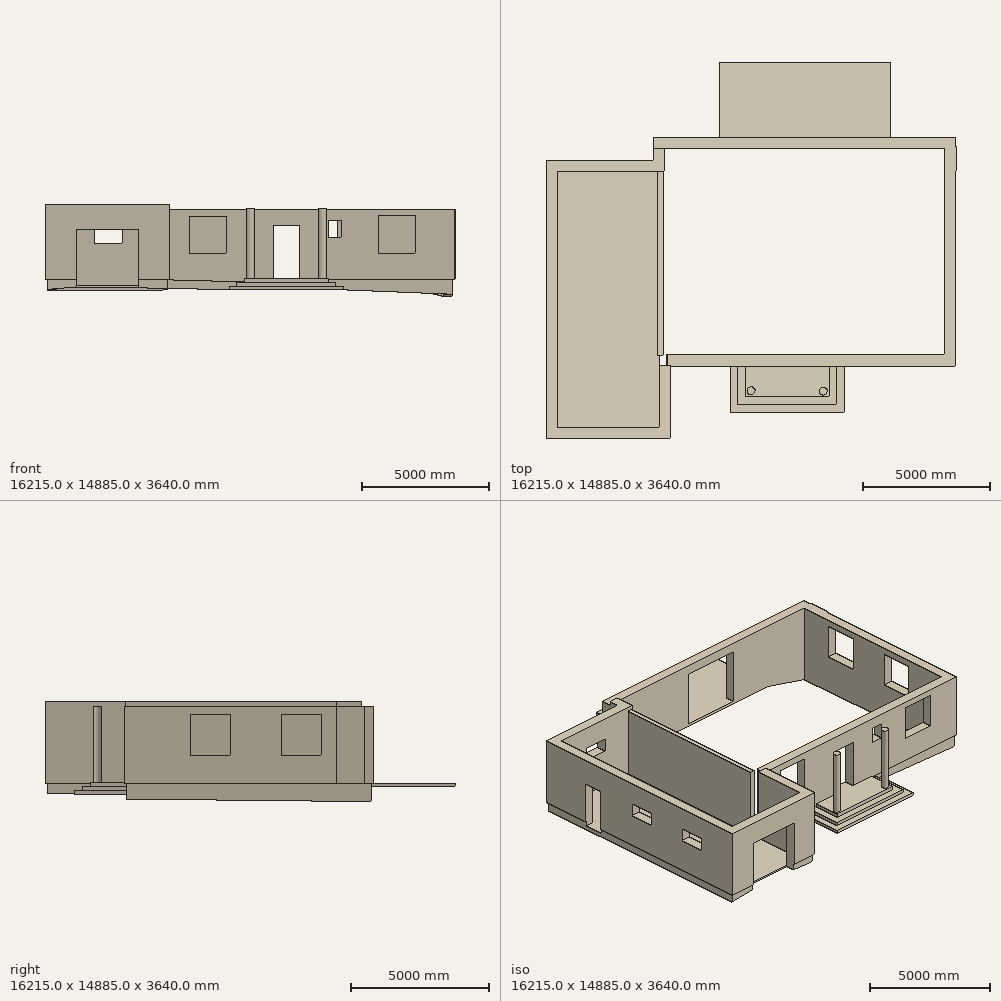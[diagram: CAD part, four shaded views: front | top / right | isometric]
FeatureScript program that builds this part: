
annotation { "Feature Type Name" : "Feature", "Feature Type Description" : "" }
export const myFeature = defineFeature(function(context is Context, id is Id, definition is map)
    precondition{}
    {
        {
            var Q0;
            Q0=qCreatedBy(makeId("Front.planeOp"),FACE);
            var sketch = newSketch(context, id + "F0", { "sketchPlane" : qUnion([Q0])});
            skLineSegment(sketch, "E0.bottom", {"start": v(0, 0) * mm, "end": v(70, 0) * mm});
            skLineSegment(sketch, "E0.top", {"start": v(0, 2980) * mm, "end": v(4455, 2980) * mm});
            skLineSegment(sketch, "E0.left", {"start": v(0, 0) * mm, "end": v(0, 2980) * mm});
            skLineSegment(sketch, "E0.right", {"start": v(4455, 0) * mm, "end": v(4455, 2980) * mm});
            skLineSegment(sketch, "E1.bottom", {"start": v(1245, 1990) * mm, "end": v(3685, 1990) * mm});
            skLineSegment(sketch, "E1.top", {"start": v(1245, -180) * mm, "end": v(3685, -180) * mm});
            skLineSegment(sketch, "E1.left", {"start": v(1245, 1990) * mm, "end": v(1245, 0) * mm});
            skLineSegment(sketch, "E1.right", {"start": v(3685, 1990) * mm, "end": v(3685, 0) * mm});
            skLineSegment(sketch, "E2", {"start": v(1245, 0) * mm, "end": v(1245, -180) * mm});
            skLineSegment(sketch, "E3", {"start": v(3685, 0) * mm, "end": v(4455, 0) * mm});
            skLineSegment(sketch, "E4", {"start": v(3685, 0) * mm, "end": v(3685, -180) * mm});
            skLineSegment(sketch, "E5", {"start": v(70, -380) * mm, "end": v(1245, -280) * mm});
            skLineSegment(sketch, "E6", {"start": v(1245, -280) * mm, "end": v(1245, -180) * mm});
            skLineSegment(sketch, "E7", {"start": v(3685, -180) * mm, "end": v(3685, -300) * mm});
            skLineSegment(sketch, "E8", {"start": v(3685, -300) * mm, "end": v(4455, -350) * mm});
            skLineSegment(sketch, "E9", {"start": v(70, 0) * mm, "end": v(1245, 0) * mm});
            skLineSegment(sketch, "E10", {"start": v(70, 0) * mm, "end": v(70, -380) * mm});
            skLineSegment(sketch, "E11", {"start": v(4455, 0) * mm, "end": v(4455, -350) * mm});
            skSolve(sketch);
        }
        {
            var Q0;
            Q0=makeQuery(id+"F0.imprint","IMPRINT",FACE,{"disambiguationData":[TD([[makeQuery(id+"F0.imprint","IMPRINT",EDGE,{"derivedFrom":sQuery(id+"F0.wireOp",EDGE,"E0.bottom")}),1.0]])]});
            extrude(context, id + "F1", {"entities" : qUnion([Q0]), "depth" : 440 * mm});
        }
        {
            var Q0;
            Q0=makeQuery(id+"F0.imprint","IMPRINT",FACE,{"disambiguationData":[TD([[makeQuery(id+"F0.imprint","IMPRINT",EDGE,{"derivedFrom":sQuery(id+"F0.wireOp",EDGE,"E2")}),-1.0]])]});
            var Q1;
            Q1=makeQuery(id+"F0.imprint","IMPRINT",FACE,{"disambiguationData":[TD([[makeQuery(id+"F0.imprint","IMPRINT",EDGE,{"derivedFrom":sQuery(id+"F0.wireOp",EDGE,"E3")}),-1.0]])]});
            extrude(context, id + "F2", {"entities" : qUnion([Q0, Q1]), "operationType" : NewBodyOperationType.ADD, "depth" : 370 * mm});
        }
        {
            var Q0;
            Q0=makeQuery(id+"F2.opExtrude","SWEPT_FACE",FACE,{"disambiguationData":[OSD([sQuery(id+"F0.wireOp",EDGE,"E10")])]});
            var sketch = newSketch(context, id + "F3", { "sketchPlane" : qUnion([Q0])});
            skLineSegment(sketch, "E12.bottom", {"start": v(440, 2980) * mm, "end": v(-10130, 2980) * mm});
            skLineSegment(sketch, "E12.top", {"start": v(440, 0) * mm, "end": v(-7385, 0) * mm});
            skLineSegment(sketch, "E12.left", {"start": v(440, 2980) * mm, "end": v(440, 0) * mm});
            skLineSegment(sketch, "E12.right", {"start": v(-10130, 2980) * mm, "end": v(-10130, 0) * mm});
            skLineSegment(sketch, "E13", {"start": v(-8275, 0) * mm, "end": v(-10130, 0) * mm});
            skLineSegment(sketch, "E14.bottom", {"start": v(-2510, 2005) * mm, "end": v(-1400, 2005) * mm});
            skLineSegment(sketch, "E14.top", {"start": v(-2510, 1445) * mm, "end": v(-1400, 1445) * mm});
            skLineSegment(sketch, "E14.left", {"start": v(-2510, 2005) * mm, "end": v(-2510, 1445) * mm});
            skLineSegment(sketch, "E14.right", {"start": v(-1400, 2005) * mm, "end": v(-1400, 1445) * mm});
            skLineSegment(sketch, "E15.bottom", {"start": v(-5475, 2005) * mm, "end": v(-4365, 2005) * mm});
            skLineSegment(sketch, "E15.top", {"start": v(-5475, 1445) * mm, "end": v(-4365, 1445) * mm});
            skLineSegment(sketch, "E15.left", {"start": v(-5475, 2005) * mm, "end": v(-5475, 1445) * mm});
            skLineSegment(sketch, "E15.right", {"start": v(-4365, 2005) * mm, "end": v(-4365, 1445) * mm});
            skLineSegment(sketch, "E16", {"start": v(-8275, 0) * mm, "end": v(-8275, 1850) * mm});
            skLineSegment(sketch, "E17", {"start": v(-8275, 1850) * mm, "end": v(-7385, 1850) * mm});
            skLineSegment(sketch, "E18", {"start": v(-7385, 1850) * mm, "end": v(-7385, 0) * mm});
            skLineSegment(sketch, "E19", {"start": v(-8275, 0) * mm, "end": v(-8275, -220) * mm});
            skLineSegment(sketch, "E20", {"start": v(-8275, -220) * mm, "end": v(-7385, -220) * mm});
            skLineSegment(sketch, "E21", {"start": v(-7385, -220) * mm, "end": v(-7385, 0) * mm});
            skLineSegment(sketch, "E22", {"start": v(0, -380) * mm, "end": v(-10130, -410) * mm});
            skLineSegment(sketch, "E23", {"start": v(-10130, -410) * mm, "end": v(-10130, 0) * mm});
            skSolve(sketch);
        }
        {
            var Q0;
            Q0=makeQuery(id+"F3.imprint","IMPRINT",FACE,{"disambiguationData":[TD([[makeQuery(id+"F3.imprint","IMPRINT",EDGE,{"derivedFrom":sQuery(id+"F3.wireOp",EDGE,"E12.bottom")}),1.0]])]});
            extrude(context, id + "F4", {"entities" : qUnion([Q0]), "operationType" : NewBodyOperationType.ADD, "oppositeDirection" : true, "depth" : 370 * mm, "hasSecondDirection" : true, "secondDirectionOppositeDirection" : false, "secondDirectionDepth" : 70 * mm});
        }
        {
            var Q0;
            Q0=makeQuery(id+"F3.imprint","IMPRINT",FACE,{"disambiguationData":[TD([[makeQuery(id+"F3.imprint","IMPRINT",EDGE,{"derivedFrom":sQuery(id+"F3.wireOp",EDGE,"E13")}),1.0]])]});
            extrude(context, id + "F5", {"entities" : qUnion([Q0]), "operationType" : NewBodyOperationType.ADD, "oppositeDirection" : true, "depth" : 370 * mm});
        }
        {
            var Q0;
            Q0=makeQuery(id+"F5.boolean.opBoolean","MERGE",FACE,{"derivedFrom":[makeQuery(id+"F4.opExtrude","SWEPT_FACE",FACE,{"disambiguationData":[OSD([sQuery(id+"F3.wireOp",EDGE,"E12.right")])]}),makeQuery(id+"F5.opExtrude","SWEPT_FACE",FACE,{"disambiguationData":[OSD([sQuery(id+"F3.wireOp",EDGE,"E23")])]})]});
            var sketch = newSketch(context, id + "F6", { "sketchPlane" : qUnion([Q0])});
            skLineSegment(sketch, "E24.bottom", {"start": v(0, 2980) * mm, "end": v(-4225, 2980) * mm});
            skLineSegment(sketch, "E24.top", {"start": v(0, 0) * mm, "end": v(-70, 0) * mm});
            skLineSegment(sketch, "E24.left", {"start": v(0, 2980) * mm, "end": v(0, 0) * mm});
            skLineSegment(sketch, "E24.right", {"start": v(-4225, 2980) * mm, "end": v(-4225, 0) * mm});
            skLineSegment(sketch, "E25", {"start": v(-70, 0) * mm, "end": v(-4225, 0) * mm});
            skLineSegment(sketch, "E26", {"start": v(-70, -410) * mm, "end": v(-4295, -430) * mm});
            skLineSegment(sketch, "E27", {"start": v(-4295, -430) * mm, "end": v(-4295, 0) * mm});
            skLineSegment(sketch, "E28", {"start": v(-4295, 0) * mm, "end": v(-4225, 0) * mm});
            skLineSegment(sketch, "E29", {"start": v(-4225, 2980) * mm, "end": v(-4665, 2980) * mm});
            skLineSegment(sketch, "E30", {"start": v(-4665, 2980) * mm, "end": v(-4665, 0) * mm});
            skLineSegment(sketch, "E31", {"start": v(-4665, -430) * mm, "end": v(-4295, -430) * mm});
            skLineSegment(sketch, "E32.bottom", {"start": v(-3040, 2005) * mm, "end": v(-1935, 2005) * mm});
            skLineSegment(sketch, "E32.top", {"start": v(-3040, 1430) * mm, "end": v(-1935, 1430) * mm});
            skLineSegment(sketch, "E32.left", {"start": v(-3040, 2005) * mm, "end": v(-3040, 1430) * mm});
            skLineSegment(sketch, "E32.right", {"start": v(-1935, 2005) * mm, "end": v(-1935, 1430) * mm});
            skLineSegment(sketch, "E33", {"start": v(-4665, 0) * mm, "end": v(-4665, -430) * mm});
            skLineSegment(sketch, "E34", {"start": v(-4665, 0) * mm, "end": v(-4295, 0) * mm});
            skLineSegment(sketch, "E35", {"start": v(-70, 0) * mm, "end": v(-70, -410) * mm});
            skSolve(sketch);
        }
        {
            var Q0;
            {var subQ6=sQuery(id+"F6.wireOp",EDGE,"E24.top");Q0=makeQuery(id+"F6.imprint","IMPRINT",FACE,{"disambiguationData":[TD([[makeQuery(id+"F6.imprint","IMPRINT",EDGE,{"derivedFrom":subQ6}),1.0]])]});}
            var Q1;
            {var subQ1=sQuery(id+"F6.wireOp",EDGE,"E24.right");Q1=makeQuery(id+"F6.imprint","IMPRINT",FACE,{"disambiguationData":[TD([[makeQuery(id+"F6.imprint","IMPRINT",EDGE,{"derivedFrom":subQ1}),1.0]])]});}
            extrude(context, id + "F7", {"entities" : qUnion([Q0, Q1]), "operationType" : NewBodyOperationType.ADD, "depth" : 440 * mm});
        }
        {
            var Q0;
            Q0=makeQuery(id+"F6.imprint","IMPRINT",FACE,{"disambiguationData":[TD([[makeQuery(id+"F6.imprint","IMPRINT",EDGE,{"derivedFrom":sQuery(id+"F6.wireOp",EDGE,"E26")}),-1.0]])]});
            var Q1;
            {var subQ0=sQuery(id+"F6.wireOp",EDGE,"E35");Q1=makeQuery(id+"F6.imprint","IMPRINT",FACE,{"disambiguationData":[TD([[makeQuery(id+"F6.imprint","IMPRINT",EDGE,{"derivedFrom":subQ0}),1.0]])]});}
            extrude(context, id + "F8", {"entities" : qUnion([Q0, Q1]), "operationType" : NewBodyOperationType.ADD, "depth" : 370 * mm});
        }
        {
            var Q0;
            Q0=makeQuery(id+"F6.imprint","IMPRINT",FACE,{"disambiguationData":[TD([[makeQuery(id+"F6.imprint","IMPRINT",EDGE,{"derivedFrom":sQuery(id+"F6.wireOp",EDGE,"E24.right")}),-1.0]])]});
            extrude(context, id + "F9", {"entities" : qUnion([Q0]), "operationType" : NewBodyOperationType.ADD, "depth" : 900 * mm});
        }
        {
            var Q0;
            Q0=makeQuery(id+"F6.imprint","IMPRINT",FACE,{"disambiguationData":[TD([[makeQuery(id+"F6.imprint","IMPRINT",EDGE,{"derivedFrom":sQuery(id+"F6.wireOp",EDGE,"E27")}),1.0]])]});
            extrude(context, id + "F10", {"entities" : qUnion([Q0]), "operationType" : NewBodyOperationType.ADD, "depth" : 900 * mm});
        }
        {
            var Q0;
            Q0=makeQuery(id+"F9.opExtrude","SWEPT_FACE",FACE,{"disambiguationData":[OSD([sQuery(id+"F6.wireOp",EDGE,"E24.right")])]});
            var sketch = newSketch(context, id + "F11", { "sketchPlane" : qUnion([Q0])});
            skLineSegment(sketch, "E36.bottom", {"start": v(-10880, 2285) * mm, "end": v(-10690, 2285) * mm});
            skLineSegment(sketch, "E36.top", {"start": v(-10880, 520) * mm, "end": v(-10690, 520) * mm});
            skLineSegment(sketch, "E36.left", {"start": v(-10880, 2285) * mm, "end": v(-10880, 520) * mm});
            skLineSegment(sketch, "E36.right", {"start": v(-10690, 2285) * mm, "end": v(-10690, 520) * mm});
            skSolve(sketch);
        }
        {
            var Q0;
            Q0 = qSketchRegion(id + "F11", true);
            extrude(context, id + "F12", {"entities" : qUnion([Q0]), "operationType" : NewBodyOperationType.REMOVE, "oppositeDirection" : true, "depth" : 400 * mm});
        }
        {
            var Q0;
            {var subQ0=sQuery(id+"F6.wireOp",EDGE,"E34");Q0=makeQuery(id+"F10.boolean.opBoolean","MERGE",FACE,{"derivedFrom":[makeQuery(id+"F9.opExtrude","CAP_FACE",FACE,{"disambiguationData":[OSD([sQuery(id+"F6.wireOp",EDGE,"E24.right"),sQuery(id+"F6.wireOp",EDGE,"E28"),sQuery(id+"F6.wireOp",EDGE,"E29"),sQuery(id+"F6.wireOp",EDGE,"E30"),subQ0])],"isStart":false}),makeQuery(id+"F10.opExtrude","CAP_FACE",FACE,{"disambiguationData":[OSD([sQuery(id+"F6.wireOp",EDGE,"E27"),sQuery(id+"F6.wireOp",EDGE,"E31"),sQuery(id+"F6.wireOp",EDGE,"E33"),subQ0])],"isStart":false})]});}
            var sketch = newSketch(context, id + "F13", { "sketchPlane" : qUnion([Q0])});
            skLineSegment(sketch, "E37.bottom", {"start": v(-4225, 0) * mm, "end": v(-6835, 0) * mm});
            skLineSegment(sketch, "E37.left", {"start": v(-4225, 0) * mm, "end": v(-4225, 2800) * mm});
            skLineSegment(sketch, "E38", {"start": v(-13595, 0) * mm, "end": v(-15725, 0) * mm});
            skLineSegment(sketch, "E39", {"start": v(-6835, 0) * mm, "end": v(-8890, 0) * mm});
            skLineSegment(sketch, "E40", {"start": v(-11550, 0) * mm, "end": v(-13595, 0) * mm});
            skLineSegment(sketch, "E41", {"start": v(-8890, 0) * mm, "end": v(-11550, 0) * mm});
            skLineSegment(sketch, "E42", {"start": v(-11550, 0) * mm, "end": v(-11550, 2400) * mm});
            skLineSegment(sketch, "E43", {"start": v(-11550, 2400) * mm, "end": v(-8890, 2400) * mm});
            skLineSegment(sketch, "E44", {"start": v(-8890, 2400) * mm, "end": v(-8890, 0) * mm});
            skLineSegment(sketch, "E45", {"start": v(-13595, 0) * mm, "end": v(-13595, -120) * mm});
            skLineSegment(sketch, "E46", {"start": v(-13595, -120) * mm, "end": v(-6835, -120) * mm});
            skLineSegment(sketch, "E47", {"start": v(-6835, -120) * mm, "end": v(-6835, 0) * mm});
            skLineSegment(sketch, "E48", {"start": v(-6835, -120) * mm, "end": v(-4295, -430) * mm});
            skLineSegment(sketch, "E49", {"start": v(-4295, -430) * mm, "end": v(-4295, 0) * mm});
            skLineSegment(sketch, "E50", {"start": v(-15725, 0) * mm, "end": v(-15725, -660) * mm});
            skLineSegment(sketch, "E51", {"start": v(-15725, -660) * mm, "end": v(-13595, -120) * mm});
            skLineSegment(sketch, "E52", {"start": v(-15725, 0) * mm, "end": v(-15725, 2800) * mm});
            skLineSegment(sketch, "E53", {"start": v(-15725, 2800) * mm, "end": v(-4225, 2800) * mm});
            skSolve(sketch);
        }
        {
            var Q0;
            Q0=makeQuery(id+"F13.imprint","IMPRINT",FACE,{"disambiguationData":[TD([[makeQuery(id+"F13.imprint","IMPRINT",EDGE,{"derivedFrom":sQuery(id+"F13.wireOp",EDGE,"E38")}),-1.0]])]});
            var Q1;
            {var subQ1=sQuery(id+"F13.wireOp",EDGE,"E37.left");Q1=makeQuery(id+"F13.imprint","IMPRINT",FACE,{"disambiguationData":[TD([[makeQuery(id+"F13.imprint","IMPRINT",EDGE,{"derivedFrom":subQ1}),-1.0]])]});}
            extrude(context, id + "F14", {"entities" : qUnion([Q0, Q1]), "operationType" : NewBodyOperationType.ADD, "depth" : 440 * mm});
        }
        {
            var Q0;
            {var subQ0=sQuery(id+"F13.wireOp",EDGE,"E45");Q0=makeQuery(id+"F13.imprint","IMPRINT",FACE,{"disambiguationData":[TD([[makeQuery(id+"F13.imprint","IMPRINT",EDGE,{"derivedFrom":subQ0}),-1.0]])]});}
            var Q1;
            {var subQ0=sQuery(id+"F13.wireOp",EDGE,"E47");Q1=makeQuery(id+"F13.imprint","IMPRINT",FACE,{"disambiguationData":[TD([[makeQuery(id+"F13.imprint","IMPRINT",EDGE,{"derivedFrom":subQ0}),-1.0]])]});}
            var Q2;
            {var subQ0=sQuery(id+"F13.wireOp",EDGE,"E49");Q2=makeQuery(id+"F13.imprint","IMPRINT",FACE,{"disambiguationData":[TD([[makeQuery(id+"F13.imprint","IMPRINT",EDGE,{"derivedFrom":subQ0}),1.0]])]});}
            var Q3;
            {var subQ0=sQuery(id+"F13.wireOp",EDGE,"E45");Q3=makeQuery(id+"F13.imprint","IMPRINT",FACE,{"disambiguationData":[TD([[makeQuery(id+"F13.imprint","IMPRINT",EDGE,{"derivedFrom":subQ0}),-1.0]])]});}
            var Q4;
            {var subQ0=sQuery(id+"F13.wireOp",EDGE,"E47");Q4=makeQuery(id+"F13.imprint","IMPRINT",FACE,{"disambiguationData":[TD([[makeQuery(id+"F13.imprint","IMPRINT",EDGE,{"derivedFrom":subQ0}),-1.0]])]});}
            var Q5;
            {var subQ0=sQuery(id+"F13.wireOp",EDGE,"E49");Q5=makeQuery(id+"F13.imprint","IMPRINT",FACE,{"disambiguationData":[TD([[makeQuery(id+"F13.imprint","IMPRINT",EDGE,{"derivedFrom":subQ0}),1.0]])]});}
            extrude(context, id + "F15", {"entities" : qUnion([Q0, Q1, Q2, Q3, Q4, Q5]), "operationType" : NewBodyOperationType.ADD, "depth" : 370 * mm});
        }
        {
            var Q0;
            Q0=makeQuery(id+"F13.imprint","IMPRINT",FACE,{"disambiguationData":[TD([[makeQuery(id+"F13.imprint","IMPRINT",EDGE,{"derivedFrom":sQuery(id+"F13.wireOp",EDGE,"E39")}),1.0]])]});
            extrude(context, id + "F16", {"entities" : qUnion([Q0]), "operationType" : NewBodyOperationType.ADD, "depth" : 3415 * mm});
        }
        {
            var Q0;
            Q0=makeQuery(id+"F15.boolean.opBoolean","MERGE",FACE,{"derivedFrom":[makeQuery(id+"F14.opExtrude","SWEPT_FACE",FACE,{"disambiguationData":[OSD([sQuery(id+"F13.wireOp",EDGE,"E37.right")])]}),makeQuery(id+"F15.opExtrude","SWEPT_FACE",FACE,{"disambiguationData":[OSD([sQuery(id+"F13.wireOp",EDGE,"E50")])]})]});
            var sketch = newSketch(context, id + "F17", { "sketchPlane" : qUnion([Q0])});
            skLineSegment(sketch, "E54", {"start": v(11470, 0) * mm, "end": v(11130, 0) * mm});
            skLineSegment(sketch, "E55", {"start": v(11130, 0) * mm, "end": v(10120, 0) * mm});
            skLineSegment(sketch, "E56", {"start": v(10120, 0) * mm, "end": v(2870, 0) * mm});
            skLineSegment(sketch, "E57", {"start": v(2870, 0) * mm, "end": v(2870, 2800) * mm});
            skLineSegment(sketch, "E58", {"start": v(2870, 2800) * mm, "end": v(10120, 2800) * mm});
            skLineSegment(sketch, "E59", {"start": v(10120, 2800) * mm, "end": v(11130, 2800) * mm});
            skLineSegment(sketch, "E60", {"start": v(11130, 2800) * mm, "end": v(11470, 2800) * mm});
            skLineSegment(sketch, "E61", {"start": v(11470, 2800) * mm, "end": v(11470, 0) * mm});
            skLineSegment(sketch, "E62", {"start": v(11130, 2800) * mm, "end": v(11130, 0) * mm});
            skLineSegment(sketch, "E63", {"start": v(10120, 2800) * mm, "end": v(10120, 0) * mm});
            skLineSegment(sketch, "E64.bottom", {"start": v(4810, 2510) * mm, "end": v(6270, 2510) * mm});
            skLineSegment(sketch, "E64.top", {"start": v(4810, 1030) * mm, "end": v(6270, 1030) * mm});
            skLineSegment(sketch, "E64.left", {"start": v(4810, 2510) * mm, "end": v(4810, 1030) * mm});
            skLineSegment(sketch, "E64.right", {"start": v(6270, 2510) * mm, "end": v(6270, 1030) * mm});
            skLineSegment(sketch, "E65.bottom", {"start": v(8120, 2510) * mm, "end": v(9580, 2510) * mm});
            skLineSegment(sketch, "E65.top", {"start": v(8120, 1030) * mm, "end": v(9580, 1030) * mm});
            skLineSegment(sketch, "E65.left", {"start": v(8120, 2510) * mm, "end": v(8120, 1030) * mm});
            skLineSegment(sketch, "E65.right", {"start": v(9580, 2510) * mm, "end": v(9580, 1030) * mm});
            skLineSegment(sketch, "E66", {"start": v(2870, 0) * mm, "end": v(2870, -570) * mm});
            skLineSegment(sketch, "E67", {"start": v(2870, -570) * mm, "end": v(11400, -660) * mm});
            skLineSegment(sketch, "E68", {"start": v(11400, -660) * mm, "end": v(11400, 0) * mm});
            skSolve(sketch);
        }
        {
            var Q0;
            Q0=makeQuery(id+"F17.imprint","IMPRINT",FACE,{"disambiguationData":[TD([[makeQuery(id+"F17.imprint","IMPRINT",EDGE,{"derivedFrom":sQuery(id+"F17.wireOp",EDGE,"E60")}),1.0]])]});
            var Q1;
            Q1=makeQuery(id+"F17.imprint","IMPRINT",FACE,{"disambiguationData":[TD([[makeQuery(id+"F17.imprint","IMPRINT",EDGE,{"derivedFrom":sQuery(id+"F17.wireOp",EDGE,"E56")}),-1.0]])]});
            extrude(context, id + "F18", {"entities" : qUnion([Q0, Q1]), "operationType" : NewBodyOperationType.ADD, "depth" : 440 * mm});
        }
        {
            var Q0;
            {var subQ0=sQuery(id+"F17.wireOp",EDGE,"E63");Q0=makeQuery(id+"F17.imprint","IMPRINT",FACE,{"disambiguationData":[TD([[makeQuery(id+"F17.imprint","IMPRINT",EDGE,{"derivedFrom":subQ0}),1.0]])]});}
            var Q1;
            {var subQ0=sQuery(id+"F17.wireOp",EDGE,"E62");Q1=makeQuery(id+"F17.imprint","IMPRINT",FACE,{"disambiguationData":[TD([[makeQuery(id+"F17.imprint","IMPRINT",EDGE,{"derivedFrom":subQ0}),-1.0]])]});}
            extrude(context, id + "F19", {"entities" : qUnion([Q0, Q1]), "operationType" : NewBodyOperationType.ADD, "depth" : 490 * mm});
        }
        {
            var Q0;
            {var subQ6=sQuery(id+"F17.wireOp",EDGE,"E56");Q0=makeQuery(id+"F17.imprint","IMPRINT",FACE,{"disambiguationData":[TD([[makeQuery(id+"F17.imprint","IMPRINT",EDGE,{"derivedFrom":subQ6}),1.0]])]});}
            var Q1;
            {var subQ0=sQuery(id+"F17.wireOp",EDGE,"E68");Q1=makeQuery(id+"F17.imprint","IMPRINT",FACE,{"disambiguationData":[TD([[makeQuery(id+"F17.imprint","IMPRINT",EDGE,{"derivedFrom":subQ0}),-1.0]])]});}
            extrude(context, id + "F20", {"entities" : qUnion([Q0, Q1]), "operationType" : NewBodyOperationType.ADD, "depth" : 370 * mm});
        }
        {
            var Q0;
            Q0=makeQuery(id+"F20.boolean.opBoolean","MERGE",FACE,{"derivedFrom":[makeQuery(id+"F18.opExtrude","SWEPT_FACE",FACE,{"disambiguationData":[OSD([sQuery(id+"F17.wireOp",EDGE,"E57")])]}),makeQuery(id+"F20.opExtrude","SWEPT_FACE",FACE,{"disambiguationData":[OSD([sQuery(id+"F17.wireOp",EDGE,"E66")])]})]});
            var sketch = newSketch(context, id + "F21", { "sketchPlane" : qUnion([Q0])});
            skLineSegment(sketch, "E69", {"start": v(16165, 2800) * mm, "end": v(4800, 2800) * mm});
            skLineSegment(sketch, "E70", {"start": v(4800, 2800) * mm, "end": v(4800, 0) * mm});
            skLineSegment(sketch, "E71", {"start": v(4800, 0) * mm, "end": v(7865, -79.94) * mm});
            skLineSegment(sketch, "E72", {"start": v(16165, 0) * mm, "end": v(16165, 2800) * mm});
            skLineSegment(sketch, "E73.bottom", {"start": v(13155, 2530) * mm, "end": v(14625, 2530) * mm});
            skLineSegment(sketch, "E73.top", {"start": v(13155, 1050) * mm, "end": v(14625, 1050) * mm});
            skLineSegment(sketch, "E73.left", {"start": v(13155, 2530) * mm, "end": v(13155, 1050) * mm});
            skLineSegment(sketch, "E73.right", {"start": v(14625, 2530) * mm, "end": v(14625, 1050) * mm});
            skLineSegment(sketch, "E74.bottom", {"start": v(11175, 2350) * mm, "end": v(11725, 2350) * mm});
            skLineSegment(sketch, "E74.top", {"start": v(11175, 1660) * mm, "end": v(11725, 1660) * mm});
            skLineSegment(sketch, "E74.left", {"start": v(11175, 2350) * mm, "end": v(11175, 1660) * mm});
            skLineSegment(sketch, "E74.right", {"start": v(11725, 2350) * mm, "end": v(11725, 1660) * mm});
            skLineSegment(sketch, "E75.bottom", {"start": v(5705, 2510) * mm, "end": v(7165, 2510) * mm});
            skLineSegment(sketch, "E75.top", {"start": v(5705, 1030) * mm, "end": v(7165, 1030) * mm});
            skLineSegment(sketch, "E75.left", {"start": v(5705, 2510) * mm, "end": v(5705, 1030) * mm});
            skLineSegment(sketch, "E75.right", {"start": v(7165, 2510) * mm, "end": v(7165, 1030) * mm});
            skLineSegment(sketch, "E76", {"start": v(11175, 0) * mm, "end": v(16165, 0) * mm});
            skLineSegment(sketch, "E77", {"start": v(7865, -79.94) * mm, "end": v(7865, 40.06) * mm});
            skLineSegment(sketch, "E78", {"start": v(7865, 40.06) * mm, "end": v(9000, 40.06) * mm});
            skLineSegment(sketch, "E79", {"start": v(9000, 40.06) * mm, "end": v(10040, 40.06) * mm});
            skLineSegment(sketch, "E80", {"start": v(10040, 40.06) * mm, "end": v(11175, 40.06) * mm});
            skLineSegment(sketch, "E81", {"start": v(11175, 40.06) * mm, "end": v(11175, 0) * mm});
            skLineSegment(sketch, "E82", {"start": v(7865, -79.94) * mm, "end": v(7865, -109.94) * mm});
            skLineSegment(sketch, "E83", {"start": v(7865, -109.94) * mm, "end": v(11175, -109.94) * mm});
            skLineSegment(sketch, "E84", {"start": v(11175, -109.94) * mm, "end": v(11175, 0) * mm});
            skLineSegment(sketch, "E85", {"start": v(9000, 40.06) * mm, "end": v(9000, 2130.06) * mm});
            skLineSegment(sketch, "E86", {"start": v(9000, 2130.06) * mm, "end": v(10040, 2130.06) * mm});
            skLineSegment(sketch, "E87", {"start": v(10040, 2130.06) * mm, "end": v(10040, 40.06) * mm});
            skLineSegment(sketch, "E88", {"start": v(7865, -109.94) * mm, "end": v(7565, -109.94) * mm});
            skLineSegment(sketch, "E89", {"start": v(7565, -109.94) * mm, "end": v(7565, -254.94) * mm});
            skLineSegment(sketch, "E90", {"start": v(7565, -254.94) * mm, "end": v(7265, -254.94) * mm});
            skLineSegment(sketch, "E91", {"start": v(7265, -254.94) * mm, "end": v(7265, -394.94) * mm});
            skLineSegment(sketch, "E92", {"start": v(11175, -109.94) * mm, "end": v(11475, -109.94) * mm});
            skLineSegment(sketch, "E93", {"start": v(11475, -109.94) * mm, "end": v(11475, -254.94) * mm});
            skLineSegment(sketch, "E94", {"start": v(11475, -254.94) * mm, "end": v(11775, -254.94) * mm});
            skLineSegment(sketch, "E95", {"start": v(11775, -254.94) * mm, "end": v(11775, -394.94) * mm});
            skLineSegment(sketch, "E96", {"start": v(11775, -394.94) * mm, "end": v(7265, -394.94) * mm});
            skLineSegment(sketch, "E97", {"start": v(4730, -330) * mm, "end": v(7265, -394.94) * mm});
            skLineSegment(sketch, "E98", {"start": v(11775, -394.94) * mm, "end": v(16095, -570) * mm});
            skLineSegment(sketch, "E99", {"start": v(16095, -570) * mm, "end": v(16095, 0) * mm});
            skLineSegment(sketch, "E100", {"start": v(7565, -254.94) * mm, "end": v(11475, -254.94) * mm});
            skLineSegment(sketch, "E101", {"start": v(4800, 0) * mm, "end": v(4730, 0) * mm});
            skLineSegment(sketch, "E102", {"start": v(4730, 0) * mm, "end": v(4730, -330) * mm});
            skSolve(sketch);
        }
        {
            var Q0;
            {var subQ6=sQuery(id+"F21.wireOp",EDGE,"E70");Q0=makeQuery(id+"F21.imprint","IMPRINT",FACE,{"disambiguationData":[TD([[makeQuery(id+"F21.imprint","IMPRINT",EDGE,{"derivedFrom":subQ6}),1.0]])]});}
            var Q1;
            {var subQ4=sQuery(id+"F21.wireOp",EDGE,"E72");Q1=makeQuery(id+"F21.imprint","IMPRINT",FACE,{"disambiguationData":[TD([[makeQuery(id+"F21.imprint","IMPRINT",EDGE,{"derivedFrom":subQ4}),1.0]])]});}
            extrude(context, id + "F22", {"entities" : qUnion([Q0, Q1]), "operationType" : NewBodyOperationType.ADD, "depth" : 440 * mm});
        }
        {
            var Q0;
            {var subQ4=sQuery(id+"F21.wireOp",EDGE,"E84");Q0=makeQuery(id+"F21.imprint","IMPRINT",FACE,{"disambiguationData":[TD([[makeQuery(id+"F21.imprint","IMPRINT",EDGE,{"derivedFrom":subQ4}),-1.0]])]});}
            var Q1;
            {var subQ0=sQuery(id+"F21.wireOp",EDGE,"E99");Q1=makeQuery(id+"F21.imprint","IMPRINT",FACE,{"disambiguationData":[TD([[makeQuery(id+"F21.imprint","IMPRINT",EDGE,{"derivedFrom":subQ0}),-1.0]])]});}
            var Q2;
            Q2=makeQuery(id+"F21.imprint","IMPRINT",FACE,{"disambiguationData":[TD([[makeQuery(id+"F21.imprint","IMPRINT",EDGE,{"derivedFrom":sQuery(id+"F21.wireOp",EDGE,"E71")}),-1.0]])]});
            extrude(context, id + "F23", {"entities" : qUnion([Q0, Q1, Q2]), "operationType" : NewBodyOperationType.ADD, "depth" : 370 * mm});
        }
        {
            var Q0;
            Q0=makeQuery(id+"F21.imprint","IMPRINT",FACE,{"disambiguationData":[TD([[makeQuery(id+"F21.imprint","IMPRINT",EDGE,{"derivedFrom":sQuery(id+"F21.wireOp",EDGE,"E90")}),1.0]])]});
            extrude(context, id + "F24", {"entities" : qUnion([Q0]), "operationType" : NewBodyOperationType.ADD, "depth" : 2275 * mm});
        }
        {
            var Q0;
            Q0=makeQuery(id+"F21.imprint","IMPRINT",FACE,{"disambiguationData":[TD([[makeQuery(id+"F21.imprint","IMPRINT",EDGE,{"derivedFrom":sQuery(id+"F21.wireOp",EDGE,"E83")}),-1.0]])]});
            extrude(context, id + "F25", {"entities" : qUnion([Q0]), "operationType" : NewBodyOperationType.ADD, "depth" : 1965 * mm});
        }
        {
            var Q0;
            Q0=makeQuery(id+"F21.imprint","IMPRINT",FACE,{"disambiguationData":[TD([[makeQuery(id+"F21.imprint","IMPRINT",EDGE,{"derivedFrom":sQuery(id+"F21.wireOp",EDGE,"E77")}),-1.0]])]});
            extrude(context, id + "F26", {"entities" : qUnion([Q0]), "operationType" : NewBodyOperationType.ADD, "depth" : 1660 * mm});
        }
        {
            var Q0;
            Q0=makeQuery(id+"F26.opExtrude","SWEPT_FACE",FACE,{"disambiguationData":[OSD([sQuery(id+"F21.wireOp",EDGE,"E78"),sQuery(id+"F21.wireOp",EDGE,"E79"),sQuery(id+"F21.wireOp",EDGE,"E80")])]});
            var sketch = newSketch(context, id + "F27", { "sketchPlane" : qUnion([Q0])});
            skCircle(sketch, "E103", {"center": v(8095, 1455) * mm, "radius": 155 * mm});
            skCircle(sketch, "E104", {"center": v(10950, 1440) * mm, "radius": 155 * mm});
            skSolve(sketch);
        }
        {
            var Q0;
            Q0=makeQuery(id+"F27.imprint","IMPRINT",FACE,{"disambiguationData":[TD([[makeQuery(id+"F27.imprint","IMPRINT",EDGE,{"derivedFrom":sQuery(id+"F27.wireOp",EDGE,"E103")}),1.0]])]});
            var Q1;
            Q1=makeQuery(id+"F27.imprint","IMPRINT",FACE,{"disambiguationData":[TD([[makeQuery(id+"F27.imprint","IMPRINT",EDGE,{"derivedFrom":sQuery(id+"F27.wireOp",EDGE,"E104")}),1.0]])]});
            extrude(context, id + "F28", {"entities" : qUnion([Q0, Q1]), "operationType" : NewBodyOperationType.ADD, "depth" : 2765 * mm});
        }
        {
            var Q0;
            Q0=makeQuery(id+"F2.boolean.opBoolean","MERGE",FACE,{"derivedFrom":[makeQuery(id+"F1.opExtrude","SWEPT_FACE",FACE,{"disambiguationData":[OSD([sQuery(id+"F0.wireOp",EDGE,"E0.right")])]}),makeQuery(id+"F2.opExtrude","SWEPT_FACE",FACE,{"disambiguationData":[OSD([sQuery(id+"F0.wireOp",EDGE,"E11")])]})]});
            var sketch = newSketch(context, id + "F29", { "sketchPlane" : qUnion([Q0])});
            skLineSegment(sketch, "E105", {"start": v(0, 2980) * mm, "end": v(2460, 2980) * mm});
            skLineSegment(sketch, "E106", {"start": v(2460, 2980) * mm, "end": v(2460, 0) * mm});
            skLineSegment(sketch, "E107", {"start": v(2460, 0) * mm, "end": v(0, 0) * mm});
            skLineSegment(sketch, "E108", {"start": v(0, -350) * mm, "end": v(2460, -350) * mm});
            skLineSegment(sketch, "E109", {"start": v(2460, -350) * mm, "end": v(2460, 0) * mm});
            skLineSegment(sketch, "E110", {"start": v(0, 0) * mm, "end": v(-370, 0) * mm});
            skLineSegment(sketch, "E111", {"start": v(2460, -350) * mm, "end": v(2530, -350) * mm});
            skLineSegment(sketch, "E112", {"start": v(2530, -350) * mm, "end": v(2530, 0) * mm});
            skSolve(sketch);
        }
        {
            var Q0;
            {var subQ0=sQuery(id+"F29.wireOp",EDGE,"E105");Q0=makeQuery(id+"F29.imprint","IMPRINT",FACE,{"disambiguationData":[TD([[makeQuery(id+"F29.imprint","IMPRINT",EDGE,{"derivedFrom":subQ0}),-1.0]])]});}
            var Q1;
            {var subQ3=sQuery(id+"F29.wireOp",EDGE,"E110");Q1=makeQuery(id+"F29.imprint","IMPRINT",FACE,{"disambiguationData":[TD([[makeQuery(id+"F29.imprint","IMPRINT",EDGE,{"derivedFrom":subQ3}),-1.0]])]});}
            extrude(context, id + "F30", {"entities" : qUnion([Q0, Q1]), "operationType" : NewBodyOperationType.ADD, "depth" : 440 * mm});
        }
        {
            var Q0;
            {var subQ0=sQuery(id+"F29.wireOp",EDGE,"E107");Q0=makeQuery(id+"F29.imprint","IMPRINT",FACE,{"disambiguationData":[TD([[makeQuery(id+"F29.imprint","IMPRINT",EDGE,{"derivedFrom":subQ0}),1.0]])]});}
            var Q1;
            {var subQ0=sQuery(id+"F29.wireOp",EDGE,"E110");Q1=makeQuery(id+"F29.imprint","IMPRINT",FACE,{"disambiguationData":[TD([[makeQuery(id+"F29.imprint","IMPRINT",EDGE,{"derivedFrom":subQ0}),1.0]])]});}
            extrude(context, id + "F31", {"entities" : qUnion([Q0, Q1]), "operationType" : NewBodyOperationType.ADD, "depth" : 370 * mm});
        }
        {
            var Q0;
            Q0=makeQuery(id+"F5.opExtrude","SWEPT_FACE",FACE,{"disambiguationData":[OSD([sQuery(id+"F3.wireOp",EDGE,"E20")])]});
            var sketch = newSketch(context, id + "F32", { "sketchPlane" : qUnion([Q0])});
            skLineSegment(sketch, "E113", {"start": v(440, 8275) * mm, "end": v(440, 10130) * mm});
            skLineSegment(sketch, "E114", {"start": v(440, 10130) * mm, "end": v(4440, 10130) * mm});
            skLineSegment(sketch, "E115", {"start": v(4440, 10130) * mm, "end": v(4455, 0) * mm});
            skLineSegment(sketch, "E116", {"start": v(4455, 0) * mm, "end": v(440, 0) * mm});
            skLineSegment(sketch, "E117", {"start": v(440, 0) * mm, "end": v(440, 7385) * mm});
            skLineSegment(sketch, "E118", {"start": v(440, 7385) * mm, "end": v(440, 8275) * mm});
            skSolve(sketch);
        }
        {
            var Q0;
            Q0 = qSketchRegion(id + "F32", true);
            extrude(context, id + "F33", {"entities" : qUnion([Q0]), "operationType" : NewBodyOperationType.ADD, "oppositeDirection" : true, "depth" : 80 * mm});
        }
        {
            var Q0;
            Q0=makeQuery(id+"F22.boolean.opBoolean","MERGE",FACE,{"derivedFrom":[makeQuery(id+"F19.boolean.opBoolean","MERGE",FACE,{"derivedFrom":[makeQuery(id+"F18.opExtrude","SWEPT_FACE",FACE,{"disambiguationData":[OSD([sQuery(id+"F17.wireOp",EDGE,"E58")])]}),makeQuery(id+"F18.boolean.opBoolean","MERGE",FACE,{"derivedFrom":[makeQuery(id+"F14.opExtrude","SWEPT_FACE",FACE,{"disambiguationData":[OSD([sQuery(id+"F13.wireOp",EDGE,"E53")])]}),makeQuery(id+"F18.opExtrude","SWEPT_FACE",FACE,{"disambiguationData":[OSD([sQuery(id+"F17.wireOp",EDGE,"E60")])]})]}),makeQuery(id+"F19.opExtrude","SWEPT_FACE",FACE,{"disambiguationData":[OSD([sQuery(id+"F17.wireOp",EDGE,"E59")])]})]}),makeQuery(id+"F22.opExtrude","SWEPT_FACE",FACE,{"disambiguationData":[OSD([sQuery(id+"F21.wireOp",EDGE,"E69")])]})]});
            var sketch = newSketch(context, id + "F34", { "sketchPlane" : qUnion([Q0])});
            skLineSegment(sketch, "E119", {"start": v(4225, 11030) * mm, "end": v(4405, 11030) * mm, "construction": true});
            skLineSegment(sketch, "E120", {"start": v(4405, 11030) * mm, "end": v(4625, 11030) * mm});
            skLineSegment(sketch, "E121", {"start": v(4625, 11030) * mm, "end": v(4625, 10130) * mm});
            skLineSegment(sketch, "E122", {"start": v(4625, 10130) * mm, "end": v(4405, 10130) * mm});
            skLineSegment(sketch, "E123", {"start": v(4405, 10130) * mm, "end": v(4405, 11030) * mm});
            skLineSegment(sketch, "E124", {"start": v(4625, 10130) * mm, "end": v(4625, 2870) * mm});
            skLineSegment(sketch, "E125", {"start": v(4625, 2870) * mm, "end": v(4800, 2870) * mm});
            skLineSegment(sketch, "E126", {"start": v(4405, 10130) * mm, "end": v(4405, 2870) * mm});
            skLineSegment(sketch, "E127", {"start": v(4405, 2870) * mm, "end": v(4405, 2430) * mm});
            skLineSegment(sketch, "E128", {"start": v(4405, 2430) * mm, "end": v(4800, 2430) * mm});
            skLineSegment(sketch, "E129", {"start": v(4405, 2870) * mm, "end": v(4625, 2870) * mm});
            skSolve(sketch);
        }
        {
            var Q0;
            Q0=makeQuery(id+"F34.imprint","IMPRINT",FACE,{"disambiguationData":[TD([[makeQuery(id+"F34.imprint","IMPRINT",EDGE,{"derivedFrom":sQuery(id+"F34.wireOp",EDGE,"E120")}),1.0]])]});
            var Q1;
            Q1=makeQuery(id+"F34.imprint","IMPRINT",FACE,{"disambiguationData":[TD([[makeQuery(id+"F34.imprint","IMPRINT",EDGE,{"derivedFrom":sQuery(id+"F34.wireOp",EDGE,"E122")}),1.0]])]});
            var Q2;
            Q2=makeQuery(id+"F34.imprint","IMPRINT",FACE,{"disambiguationData":[TD([[makeQuery(id+"F34.imprint","IMPRINT",EDGE,{"derivedFrom":sQuery(id+"F34.wireOp",EDGE,"E125")}),-1.0]])]});
            extrude(context, id + "F35", {"entities" : qUnion([Q0, Q1, Q2]), "operationType" : NewBodyOperationType.ADD, "oppositeDirection" : true, "depth" : 3020 * mm});
        }
    });
